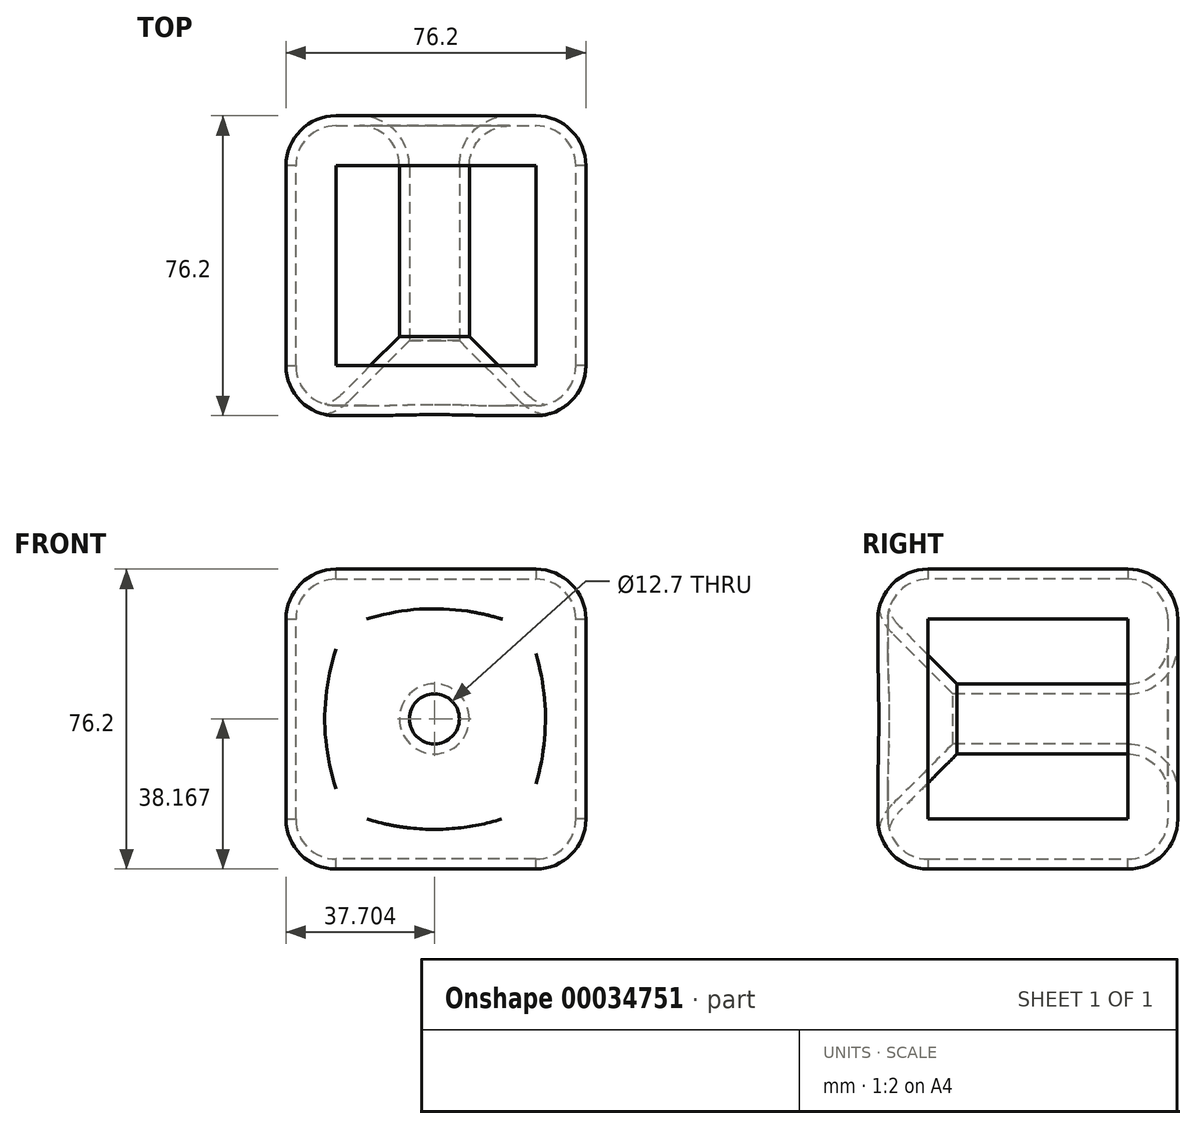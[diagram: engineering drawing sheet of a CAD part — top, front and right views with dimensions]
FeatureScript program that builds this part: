
annotation { "Feature Type Name" : "Feature", "Feature Type Description" : "" }
export const myFeature = defineFeature(function(context is Context, id is Id, definition is map)
    precondition{}
    {
        {
            var Q0;
            Q0=qCreatedBy(makeId("Right.planeOp"),FACE);
            var sketch = newSketch(context, id + "F0", { "sketchPlane" : qUnion([Q0])});
            skLineSegment(sketch, "E0.rect.bottom", {"start": v(22.63, -94.92) * mm, "end": v(-53.57, -94.92) * mm});
            skLineSegment(sketch, "E0.rect.top", {"start": v(22.63, -18.72) * mm, "end": v(-53.57, -18.72) * mm});
            skLineSegment(sketch, "E0.rect.left", {"start": v(22.63, -94.92) * mm, "end": v(22.63, -18.72) * mm});
            skLineSegment(sketch, "E0.rect.right", {"start": v(-53.57, -94.92) * mm, "end": v(-53.57, -18.72) * mm});
            skPoint(sketch, "E0.rect.middle", {"position": v(-15.47, -56.82) * mm});
            skSolve(sketch);
        }
        {
            var Q0;
            Q0=makeQuery(id+"F0.imprint","IMPRINT",FACE,{"disambiguationData":[TD([[makeQuery(id+"F0.imprint","IMPRINT",EDGE,{"derivedFrom":sQuery(id+"F0.wireOp",EDGE,"E0.rect.bottom")}),-1.0]])]});
            extrude(context, id + "F1", {"entities" : qUnion([Q0]), "depth" : 76.2 * mm});
        }
        {
            var Q0;
            Q0=makeQuery(id+"F1.opExtrude","SWEPT_FACE",FACE,{"disambiguationData":[OSD([sQuery(id+"F0.wireOp",EDGE,"E0.rect.right")])]});
            var sketch = newSketch(context, id + "F2", { "sketchPlane" : qUnion([Q0])});
            skCircle(sketch, "E1", {"center": v(37.7, -56.75) * mm, "radius": 9.66 * mm});
            skSolve(sketch);
        }
        {
            var Q0;
            Q0=sQuery(id+"F2.wireOp",VERTEX,"E1.center");
            var Q1;
            Q1=makeQuery(id+"F1.opExtrude","SWEPT_BODY",BODY,{"disambiguationData":[OSD([sQuery(id+"F0.wireOp",EDGE,"E0.rect.bottom"),sQuery(id+"F0.wireOp",EDGE,"E0.rect.top"),sQuery(id+"F0.wireOp",EDGE,"E0.rect.left"),sQuery(id+"F0.wireOp",EDGE,"E0.rect.right")])]});
            hole(context, id + "F3", {"style" : HoleStyle.C_SINK, "holeDiameter" : 12.7 * mm, "cSinkDiameter" : 50.8 * mm, "endStyle" : HoleEndStyle.THROUGH, "locations" : qUnion([Q0]), "scope" : qUnion([Q1]), "cSinkAngle" : 90 * degree});
        }
        {
            var Q0;
            Q0=makeQuery(id+"F1.opExtrude","CAP_FACE",FACE,{"disambiguationData":[OSD([sQuery(id+"F0.wireOp",EDGE,"E0.rect.bottom"),sQuery(id+"F0.wireOp",EDGE,"E0.rect.top"),sQuery(id+"F0.wireOp",EDGE,"E0.rect.left"),sQuery(id+"F0.wireOp",EDGE,"E0.rect.right")])],"isStart":true});
            var Q1;
            Q1=makeQuery(id+"F1.opExtrude","SWEPT_FACE",FACE,{"disambiguationData":[OSD([sQuery(id+"F0.wireOp",EDGE,"E0.rect.bottom")])]});
            var Q2;
            Q2=makeQuery(id+"F1.opExtrude","SWEPT_FACE",FACE,{"disambiguationData":[OSD([sQuery(id+"F0.wireOp",EDGE,"E0.rect.right")])]});
            var Q3;
            Q3=makeQuery(id+"F1.opExtrude","CAP_FACE",FACE,{"disambiguationData":[OSD([sQuery(id+"F0.wireOp",EDGE,"E0.rect.bottom"),sQuery(id+"F0.wireOp",EDGE,"E0.rect.top"),sQuery(id+"F0.wireOp",EDGE,"E0.rect.left"),sQuery(id+"F0.wireOp",EDGE,"E0.rect.right")])],"isStart":false});
            var Q4;
            Q4=makeQuery(id+"F1.opExtrude","SWEPT_FACE",FACE,{"disambiguationData":[OSD([sQuery(id+"F0.wireOp",EDGE,"E0.rect.left")])]});
            var Q5;
            Q5=makeQuery(id+"F1.opExtrude","SWEPT_FACE",FACE,{"disambiguationData":[OSD([sQuery(id+"F0.wireOp",EDGE,"E0.rect.top")])]});
            fillet(context, id + "F4", {"entities" : qUnion([Q0, Q1, Q2, Q3, Q4, Q5]), "radius" : 12.7 * mm, "tangentPropagation" : true, "allowEdgeOverflow" : false});
        }
        {
            var Q0;
            Q0=makeQuery(id+"F1.opExtrude","CAP_FACE",FACE,{"disambiguationData":[OSD([sQuery(id+"F0.wireOp",EDGE,"E0.rect.bottom"),sQuery(id+"F0.wireOp",EDGE,"E0.rect.top"),sQuery(id+"F0.wireOp",EDGE,"E0.rect.left"),sQuery(id+"F0.wireOp",EDGE,"E0.rect.right")])],"isStart":false});
            var Q1;
            Q1=makeQuery(id+"F1.opExtrude","SWEPT_FACE",FACE,{"disambiguationData":[OSD([sQuery(id+"F0.wireOp",EDGE,"E0.rect.top")])]});
            var Q2;
            Q2=makeQuery(id+"F1.opExtrude","SWEPT_FACE",FACE,{"disambiguationData":[OSD([sQuery(id+"F0.wireOp",EDGE,"E0.rect.bottom")])]});
            var Q3;
            Q3=makeQuery(id+"F1.opExtrude","CAP_FACE",FACE,{"disambiguationData":[OSD([sQuery(id+"F0.wireOp",EDGE,"E0.rect.bottom"),sQuery(id+"F0.wireOp",EDGE,"E0.rect.top"),sQuery(id+"F0.wireOp",EDGE,"E0.rect.left"),sQuery(id+"F0.wireOp",EDGE,"E0.rect.right")])],"isStart":true});
            shell(context, id + "F5", {"entities" : qUnion([Q0, Q1, Q2, Q3]), "thickness" : 2.54 * mm});
        }
    });
